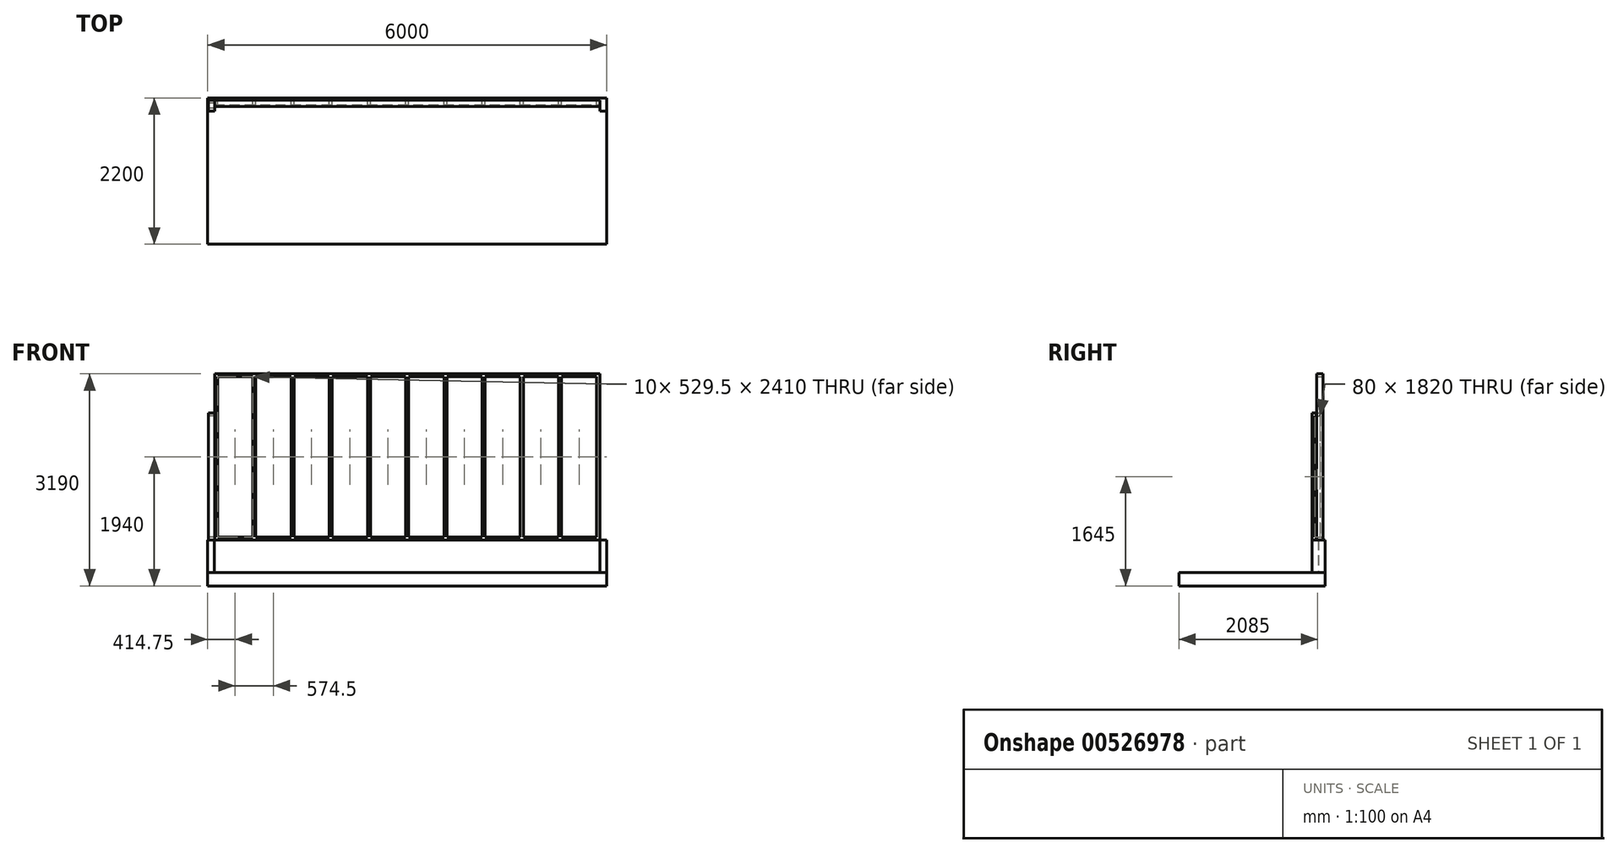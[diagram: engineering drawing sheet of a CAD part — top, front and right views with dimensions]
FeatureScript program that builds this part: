
annotation { "Feature Type Name" : "Feature", "Feature Type Description" : "" }
export const myFeature = defineFeature(function(context is Context, id is Id, definition is map)
    precondition{}
    {
        {
            var Q0;
            Q0=qCreatedBy(makeId("Top.planeOp"),FACE);
            var Q1;
            Q1=qCreatedBy(makeId("Top.planeOp"),FACE);
            var Q2;
            Q2=qCreatedBy(makeId("Top.planeOp"),FACE);
            var sketch = newSketch(context, id + "F0", { "sketchPlane" : qUnion([Q0, Q1, Q2])});
            skLineSegment(sketch, "E0", {"start": v(0, 0) * mm, "end": v(0, -200) * mm});
            skLineSegment(sketch, "E1", {"start": v(0, -200) * mm, "end": v(100, -200) * mm});
            skLineSegment(sketch, "E2", {"start": v(100, -200) * mm, "end": v(100, -100) * mm});
            skLineSegment(sketch, "E3", {"start": v(100, -100) * mm, "end": v(5900, -100) * mm});
            skLineSegment(sketch, "E4", {"start": v(5900, -100) * mm, "end": v(5900, -200) * mm});
            skLineSegment(sketch, "E5", {"start": v(5900, -200) * mm, "end": v(6000, -200) * mm});
            skLineSegment(sketch, "E6", {"start": v(6000, -200) * mm, "end": v(6000, 0) * mm});
            skLineSegment(sketch, "E7", {"start": v(6000, 0) * mm, "end": v(0, 0) * mm});
            skLineSegment(sketch, "E8", {"start": v(100, -100) * mm, "end": v(100, 0) * mm, "construction": true});
            skLineSegment(sketch, "E9", {"start": v(0, -200) * mm, "end": v(0, -2200) * mm});
            skLineSegment(sketch, "E10", {"start": v(0, -2200) * mm, "end": v(6000, -2200) * mm});
            skLineSegment(sketch, "E11", {"start": v(6000, -2200) * mm, "end": v(6000, -200) * mm});
            skSolve(sketch);
        }
        {
            var Q0;
            Q0=qCreatedBy(makeId("Top.planeOp"),FACE);
            var Q1;
            Q1=qCreatedBy(makeId("Top.planeOp"),FACE);
            var sketch = newSketch(context, id + "F1", { "sketchPlane" : qUnion([Q0, Q1])});
            skLineSegment(sketch, "E12", {"start": v(10, -30) * mm, "end": v(10, -200) * mm});
            skLineSegment(sketch, "E13", {"start": v(10, -200) * mm, "end": v(105, -200) * mm});
            skLineSegment(sketch, "E14", {"start": v(105, -200) * mm, "end": v(105, -125) * mm});
            skLineSegment(sketch, "E15", {"start": v(105, -125) * mm, "end": v(5895, -125) * mm});
            skLineSegment(sketch, "E16", {"start": v(5895, -125) * mm, "end": v(5895, -200) * mm});
            skLineSegment(sketch, "E17", {"start": v(5895, -200) * mm, "end": v(5990, -200) * mm});
            skLineSegment(sketch, "E18", {"start": v(5990, -200) * mm, "end": v(5990, -30) * mm});
            skLineSegment(sketch, "E19", {"start": v(5990, -30) * mm, "end": v(10, -30) * mm});
            skLineSegment(sketch, "E20", {"start": v(105, -125) * mm, "end": v(105, -30) * mm, "construction": true});
            skSolve(sketch);
        }
        {
            var Q0;
            Q0=qCreatedBy(makeId("Right.planeOp"),FACE);
            var Q1;
            Q1=qCreatedBy(makeId("Right.planeOp"),FACE);
            var sketch = newSketch(context, id + "F2", { "sketchPlane" : qUnion([Q0, Q1])});
            skLineSegment(sketch, "E21.bottom", {"start": v(0, 0) * mm, "end": v(-2200, 0) * mm});
            skLineSegment(sketch, "E21.top", {"start": v(0, -200) * mm, "end": v(-2200, -200) * mm});
            skLineSegment(sketch, "E21.left", {"start": v(0, 0) * mm, "end": v(0, -200) * mm});
            skLineSegment(sketch, "E21.right", {"start": v(-2200, 0) * mm, "end": v(-2200, -200) * mm});
            skLineSegment(sketch, "E22.bottom", {"start": v(0, 490) * mm, "end": v(-200, 490) * mm});
            skLineSegment(sketch, "E22.top", {"start": v(0, 0) * mm, "end": v(-200, 0) * mm});
            skLineSegment(sketch, "E22.left", {"start": v(0, 490) * mm, "end": v(0, 0) * mm});
            skLineSegment(sketch, "E22.right", {"start": v(-200, 490) * mm, "end": v(-200, 0) * mm});
            skLineSegment(sketch, "E23.bottom", {"start": v(-200, 2400) * mm, "end": v(-30, 2400) * mm});
            skLineSegment(sketch, "E23.top", {"start": v(-200, 490) * mm, "end": v(-30, 490) * mm});
            skLineSegment(sketch, "E23.left", {"start": v(-200, 2400) * mm, "end": v(-200, 490) * mm});
            skLineSegment(sketch, "E23.right", {"start": v(-30, 2400) * mm, "end": v(-30, 490) * mm});
            skPoint(sketch, "E23.middle", {"position": v(-115, 1445) * mm});
            skLineSegment(sketch, "E24.bottom", {"start": v(-155, 2355) * mm, "end": v(-75, 2355) * mm});
            skLineSegment(sketch, "E24.top", {"start": v(-155, 535) * mm, "end": v(-75, 535) * mm});
            skLineSegment(sketch, "E24.left", {"start": v(-155, 2355) * mm, "end": v(-155, 535) * mm});
            skLineSegment(sketch, "E24.right", {"start": v(-75, 2355) * mm, "end": v(-75, 535) * mm});
            skSolve(sketch);
        }
        {
            var Q0;
            Q0=qCreatedBy(makeId("Front.planeOp"),FACE);
            var sketch = newSketch(context, id + "F3", { "sketchPlane" : qUnion([Q0])});
            skLineSegment(sketch, "E25.bottom", {"start": v(5895, 490) * mm, "end": v(105, 490) * mm});
            skLineSegment(sketch, "E25.top", {"start": v(5895, 2990) * mm, "end": v(105, 2990) * mm});
            skLineSegment(sketch, "E25.left", {"start": v(5895, 490) * mm, "end": v(5895, 2990) * mm});
            skLineSegment(sketch, "E25.right", {"start": v(105, 490) * mm, "end": v(105, 2990) * mm});
            skPoint(sketch, "E25.middle", {"position": v(3000, 1740) * mm});
            skLineSegment(sketch, "E26.bottom", {"start": v(679.5, 535) * mm, "end": v(150, 535) * mm});
            skLineSegment(sketch, "E26.top", {"start": v(679.5, 2945) * mm, "end": v(150, 2945) * mm});
            skLineSegment(sketch, "E26.left", {"start": v(679.5, 535) * mm, "end": v(679.5, 2945) * mm});
            skLineSegment(sketch, "E26.right", {"start": v(150, 535) * mm, "end": v(150, 2945) * mm});
            skPoint(sketch, "E26.middle", {"position": v(414.75, 1740) * mm});
            skLineSegment(sketch, "E27.1.0.0", {"start": v(724.5, 535) * mm, "end": v(724.5, 2945) * mm});
            skLineSegment(sketch, "E27.1.0.1", {"start": v(1254, 2945) * mm, "end": v(724.5, 2945) * mm});
            skLineSegment(sketch, "E27.1.0.2", {"start": v(1254, 535) * mm, "end": v(1254, 2945) * mm});
            skLineSegment(sketch, "E27.1.0.3", {"start": v(1254, 535) * mm, "end": v(724.5, 535) * mm});
            skLineSegment(sketch, "E27.2.0.0", {"start": v(1299, 535) * mm, "end": v(1299, 2945) * mm});
            skLineSegment(sketch, "E27.2.0.1", {"start": v(1828.5, 2945) * mm, "end": v(1299, 2945) * mm});
            skLineSegment(sketch, "E27.2.0.2", {"start": v(1828.5, 535) * mm, "end": v(1828.5, 2945) * mm});
            skLineSegment(sketch, "E27.2.0.3", {"start": v(1828.5, 535) * mm, "end": v(1299, 535) * mm});
            skLineSegment(sketch, "E27.3.0.0", {"start": v(1873.5, 535) * mm, "end": v(1873.5, 2945) * mm});
            skLineSegment(sketch, "E27.3.0.1", {"start": v(2403, 2945) * mm, "end": v(1873.5, 2945) * mm});
            skLineSegment(sketch, "E27.3.0.2", {"start": v(2403, 535) * mm, "end": v(2403, 2945) * mm});
            skLineSegment(sketch, "E27.3.0.3", {"start": v(2403, 535) * mm, "end": v(1873.5, 535) * mm});
            skLineSegment(sketch, "E27.4.0.0", {"start": v(2448, 535) * mm, "end": v(2448, 2945) * mm});
            skLineSegment(sketch, "E27.4.0.1", {"start": v(2977.5, 2945) * mm, "end": v(2448, 2945) * mm});
            skLineSegment(sketch, "E27.4.0.2", {"start": v(2977.5, 535) * mm, "end": v(2977.5, 2945) * mm});
            skLineSegment(sketch, "E27.4.0.3", {"start": v(2977.5, 535) * mm, "end": v(2448, 535) * mm});
            skLineSegment(sketch, "E27.5.0.0", {"start": v(3022.5, 535) * mm, "end": v(3022.5, 2945) * mm});
            skLineSegment(sketch, "E27.5.0.1", {"start": v(3552, 2945) * mm, "end": v(3022.5, 2945) * mm});
            skLineSegment(sketch, "E27.5.0.2", {"start": v(3552, 535) * mm, "end": v(3552, 2945) * mm});
            skLineSegment(sketch, "E27.5.0.3", {"start": v(3552, 535) * mm, "end": v(3022.5, 535) * mm});
            skLineSegment(sketch, "E27.6.0.0", {"start": v(3597, 535) * mm, "end": v(3597, 2945) * mm});
            skLineSegment(sketch, "E27.6.0.1", {"start": v(4126.5, 2945) * mm, "end": v(3597, 2945) * mm});
            skLineSegment(sketch, "E27.6.0.2", {"start": v(4126.5, 535) * mm, "end": v(4126.5, 2945) * mm});
            skLineSegment(sketch, "E27.6.0.3", {"start": v(4126.5, 535) * mm, "end": v(3597, 535) * mm});
            skLineSegment(sketch, "E27.7.0.0", {"start": v(4171.5, 535) * mm, "end": v(4171.5, 2945) * mm});
            skLineSegment(sketch, "E27.7.0.1", {"start": v(4701, 2945) * mm, "end": v(4171.5, 2945) * mm});
            skLineSegment(sketch, "E27.7.0.2", {"start": v(4701, 535) * mm, "end": v(4701, 2945) * mm});
            skLineSegment(sketch, "E27.7.0.3", {"start": v(4701, 535) * mm, "end": v(4171.5, 535) * mm});
            skLineSegment(sketch, "E27.8.0.0", {"start": v(4746, 535) * mm, "end": v(4746, 2945) * mm});
            skLineSegment(sketch, "E27.8.0.1", {"start": v(5275.5, 2945) * mm, "end": v(4746, 2945) * mm});
            skLineSegment(sketch, "E27.8.0.2", {"start": v(5275.5, 535) * mm, "end": v(5275.5, 2945) * mm});
            skLineSegment(sketch, "E27.8.0.3", {"start": v(5275.5, 535) * mm, "end": v(4746, 535) * mm});
            skLineSegment(sketch, "E27.9.0.0", {"start": v(5320.5, 535) * mm, "end": v(5320.5, 2945) * mm});
            skLineSegment(sketch, "E27.9.0.1", {"start": v(5850, 2945) * mm, "end": v(5320.5, 2945) * mm});
            skLineSegment(sketch, "E27.9.0.2", {"start": v(5850, 535) * mm, "end": v(5850, 2945) * mm});
            skLineSegment(sketch, "E27.9.0.3", {"start": v(5850, 535) * mm, "end": v(5320.5, 535) * mm});
            skLineSegment(sketch, "E27.direction1", {"start": v(150, 535) * mm, "end": v(724.5, 535) * mm, "construction": true});
            skSolve(sketch);
        }
        {
            var Q0;
            Q0=makeQuery(id+"F0.imprint","IMPRINT",FACE,{"disambiguationData":[TD([[makeQuery(id+"F0.imprint","IMPRINT",EDGE,{"derivedFrom":sQuery(id+"F0.wireOp",EDGE,"E1")}),-1.0]])]});
            var Q1;
            Q1=makeQuery(id+"F0.imprint","IMPRINT",FACE,{"disambiguationData":[TD([[makeQuery(id+"F0.imprint","IMPRINT",EDGE,{"derivedFrom":sQuery(id+"F0.wireOp",EDGE,"E0")}),1.0]])]});
            var Q2;
            Q2=sQuery(id+"F2.wireOp",VERTEX,"E21.top.start");
            extrude(context, id + "F4", {"entities" : qUnion([Q0, Q1]), "endBound" : BoundingType.UP_TO_VERTEX, "oppositeDirection" : true, "depth" : 25 * mm, "endBoundEntityVertex" : qUnion([Q2]), "offsetDistance" : 25 * mm});
        }
        {
            var Q0;
            Q0=makeQuery(id+"F0.imprint","IMPRINT",FACE,{"disambiguationData":[TD([[makeQuery(id+"F0.imprint","IMPRINT",EDGE,{"derivedFrom":sQuery(id+"F0.wireOp",EDGE,"E0")}),1.0]])]});
            var Q1;
            Q1=sQuery(id+"F2.wireOp",VERTEX,"E22.bottom.start");
            extrude(context, id + "F5", {"entities" : qUnion([Q0]), "endBound" : BoundingType.UP_TO_VERTEX, "depth" : 25 * mm, "endBoundEntityVertex" : qUnion([Q1]), "offsetDistance" : 25 * mm});
        }
        {
            var Q0;
            Q0=makeQuery(id+"F2.imprint","IMPRINT",FACE,{"disambiguationData":[TD([[makeQuery(id+"F2.imprint","IMPRINT",EDGE,{"derivedFrom":sQuery(id+"F2.wireOp",EDGE,"E23.bottom")}),-1.0]])]});
            var Q1;
            Q1=sQuery(id+"F1.wireOp",VERTEX,"E13.end");
            var Q2;
            Q2=sQuery(id+"F1.wireOp",VERTEX,"E12.end");
            extrude(context, id + "F6", {"entities" : qUnion([Q0]), "endBound" : BoundingType.UP_TO_VERTEX, "depth" : 25 * mm, "endBoundEntityVertex" : qUnion([Q1]), "offsetDistance" : 25 * mm, "hasSecondDirection" : true, "secondDirectionBound" : SecondDirectionBoundingType.UP_TO_VERTEX, "secondDirectionOppositeDirection" : false, "secondDirectionDepth" : 25 * mm, "secondDirectionBoundEntityVertex" : qUnion([Q2])});
        }
        {
            var Q0;
            Q0=makeQuery(id+"F3.imprint","IMPRINT",FACE,{"disambiguationData":[TD([[makeQuery(id+"F3.imprint","IMPRINT",EDGE,{"derivedFrom":sQuery(id+"F3.wireOp",EDGE,"E25.bottom")}),-1.0]])]});
            var Q1;
            Q1=sQuery(id+"F1.wireOp",VERTEX,"E14.end");
            var Q2;
            Q2=sQuery(id+"F1.wireOp",VERTEX,"E20.end");
            extrude(context, id + "F7", {"entities" : qUnion([Q0]), "endBound" : BoundingType.UP_TO_VERTEX, "depth" : 25 * mm, "endBoundEntityVertex" : qUnion([Q1]), "offsetDistance" : 25 * mm, "hasSecondDirection" : true, "secondDirectionBound" : SecondDirectionBoundingType.UP_TO_VERTEX, "secondDirectionOppositeDirection" : false, "secondDirectionDepth" : 25 * mm, "secondDirectionBoundEntityVertex" : qUnion([Q2])});
        }
    });
